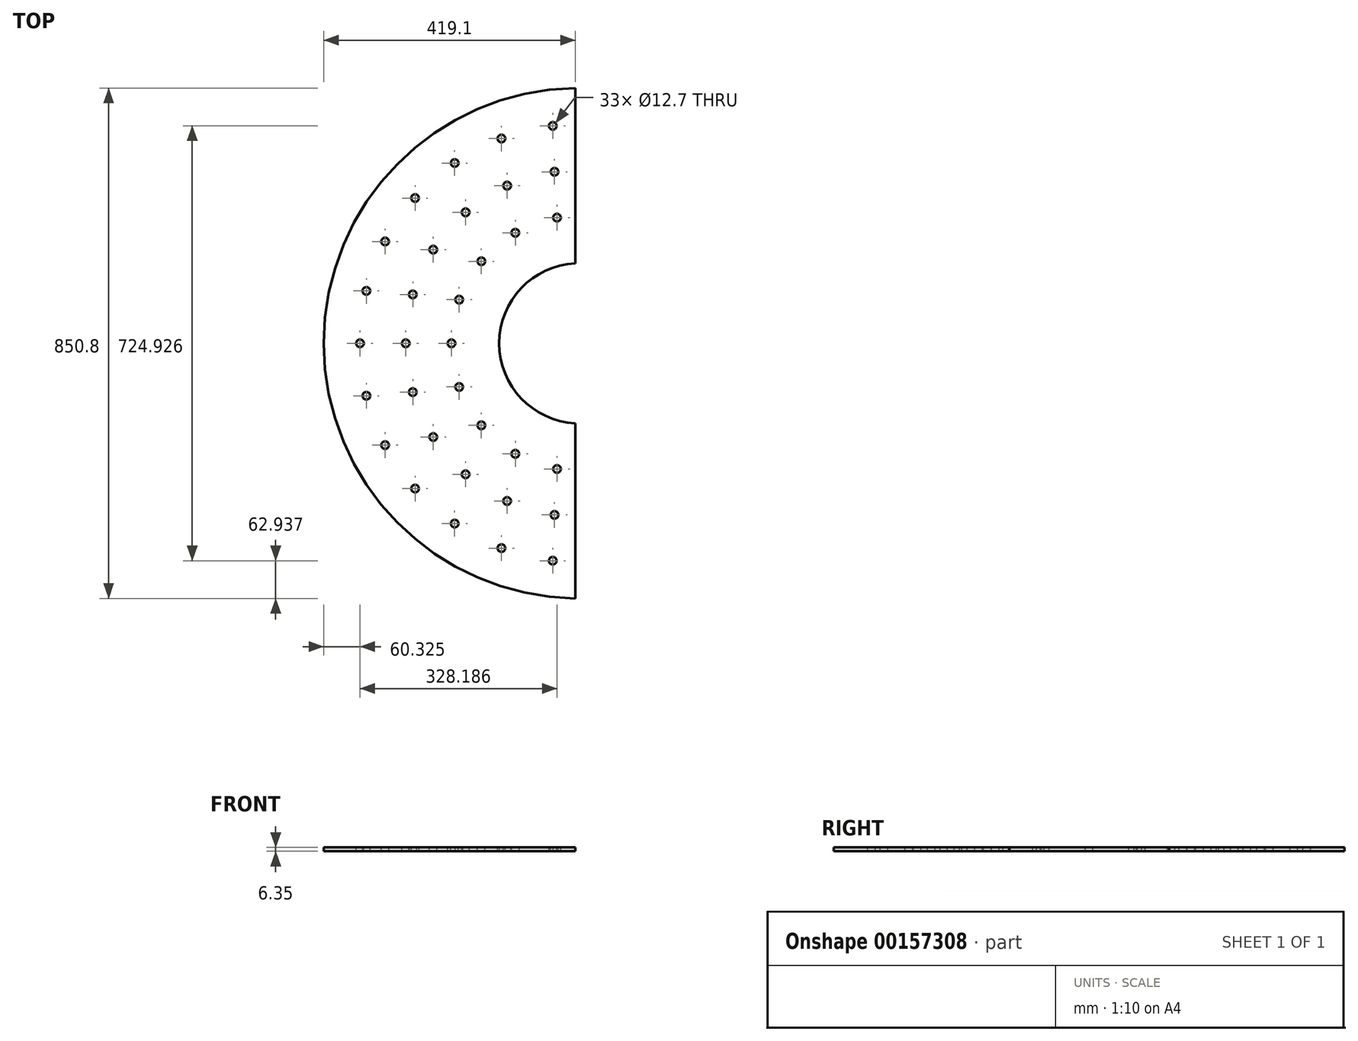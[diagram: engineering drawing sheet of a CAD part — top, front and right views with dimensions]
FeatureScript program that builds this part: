
annotation { "Feature Type Name" : "Feature", "Feature Type Description" : "" }
export const myFeature = defineFeature(function(context is Context, id is Id, definition is map)
    precondition{}
    {
        {
            var Q0;
            Q0=qCreatedBy(makeId("Top.planeOp"),FACE);
            var sketch = newSketch(context, id + "F0", { "sketchPlane" : qUnion([Q0])});
            skCircle(sketch, "E0", {"center": v(0, 0) * mm, "radius": 133.35 * mm});
            skCircle(sketch, "E1", {"center": v(0, 0) * mm, "radius": 425.45 * mm});
            skLineSegment(sketch, "E2", {"start": v(0, 133.35) * mm, "end": v(0, 425.45) * mm});
            skLineSegment(sketch, "E3", {"start": v(0, -133.35) * mm, "end": v(0, -425.45) * mm});
            skArc(sketch, "E4", {"start": v(0, -133.35) * mm, "mid": v(133.35, 0) * mm, "end": v(0, 133.35) * mm});
            skArc(sketch, "E5", {"start": v(0, -425.45) * mm, "mid": v(425.45, 0) * mm, "end": v(0, 425.45) * mm});
            skSolve(sketch);
        }
        {
            var Q0;
            Q0 = qSketchRegion(id + "F0", true);
            extrude(context, id + "F1", {"entities" : qUnion([Q0]), "depth" : 6.35 * mm});
        }
        {
            var Q0;
            Q0=makeQuery(id+"F1.opExtrude","CAP_FACE",FACE,{"disambiguationData":[OSD([sQuery(id+"F0.wireOp",EDGE,"E0"),sQuery(id+"F0.wireOp",EDGE,"E1")])],"isStart":false});
            var sketch = newSketch(context, id + "F2", { "sketchPlane" : qUnion([Q0])});
            skLineSegment(sketch, "E6", {"start": v(0, 133.35) * mm, "end": v(0, 425.45) * mm});
            skLineSegment(sketch, "E7", {"start": v(0, -133.35) * mm, "end": v(0, -425.45) * mm});
            skArc(sketch, "E8", {"start": v(0, -425.45) * mm, "mid": v(425.45, 0) * mm, "end": v(0, 425.45) * mm});
            skArc(sketch, "E9", {"start": v(0, -133.35) * mm, "mid": v(133.35, 0) * mm, "end": v(0, 133.35) * mm});
            skSolve(sketch);
        }
        {
            var Q0;
            Q0 = qSketchRegion(id + "F2", true);
            extrude(context, id + "F3", {"entities" : qUnion([Q0]), "operationType" : NewBodyOperationType.REMOVE, "endBound" : BoundingType.THROUGH_ALL, "oppositeDirection" : true, "depth" : 25.4 * mm});
        }
        {
            var Q0;
            Q0=makeQuery(id+"F1.opExtrude","CAP_FACE",FACE,{"disambiguationData":[OSD([sQuery(id+"F0.wireOp",EDGE,"E0"),sQuery(id+"F0.wireOp",EDGE,"E1")])],"isStart":false});
            var sketch = newSketch(context, id + "F4", { "sketchPlane" : qUnion([Q0])});
            skLineSegment(sketch, "E10.0", {"start": v(-31.75, 162.02) * mm, "end": v(-31.75, 392.42) * mm});
            skArc(sketch, "E10.1", {"start": v(-31.75, 162.02) * mm, "mid": v(-165.1, 0) * mm, "end": v(-31.75, -162.02) * mm});
            skLineSegment(sketch, "E10.2", {"start": v(-31.75, -162.02) * mm, "end": v(-31.75, -392.42) * mm});
            skArc(sketch, "E10.3", {"start": v(-31.75, 392.42) * mm, "mid": v(-393.7, 0) * mm, "end": v(-31.75, -392.42) * mm});
            skSolve(sketch);
        }
        {
            var Q0;
            Q0=makeQuery(id+"F4.imprint","IMPRINT",FACE,{"disambiguationData":[TD([[makeQuery(id+"F4.imprint","IMPRINT",EDGE,{"derivedFrom":sQuery(id+"F4.wireOp",EDGE,"E10.0")}),1.0]])]});
            var sketch = newSketch(context, id + "F5", { "sketchPlane" : qUnion([Q0])});
            skCircle(sketch, "E11", {"center": v(-288.93, 0) * mm, "radius": 6.35 * mm});
            skCircle(sketch, "E12.1.0", {"center": v(-277.22, -81.4) * mm, "radius": 6.35 * mm});
            skCircle(sketch, "E12.2.0", {"center": v(-243.06, -156.2) * mm, "radius": 6.35 * mm});
            skCircle(sketch, "E12.3.0", {"center": v(-189.2, -218.35) * mm, "radius": 6.35 * mm});
            skCircle(sketch, "E12.4.0", {"center": v(-120.02, -262.82) * mm, "radius": 6.35 * mm});
            skCircle(sketch, "E12.5.0", {"center": v(-41.12, -285.98) * mm, "radius": 6.35 * mm});
            skCircle(sketch, "E12.6.0", {"center": v(41.12, -285.98) * mm, "radius": 6.35 * mm});
            skCircle(sketch, "E12.7.0", {"center": v(120.02, -262.82) * mm, "radius": 6.35 * mm});
            skCircle(sketch, "E12.8.0", {"center": v(189.2, -218.35) * mm, "radius": 6.35 * mm});
            skCircle(sketch, "E12.9.0", {"center": v(243.06, -156.2) * mm, "radius": 6.35 * mm});
            skCircle(sketch, "E12.10.0", {"center": v(277.22, -81.4) * mm, "radius": 6.35 * mm});
            skCircle(sketch, "E12.11.0", {"center": v(288.93, 0) * mm, "radius": 6.35 * mm});
            skCircle(sketch, "E12.12.0", {"center": v(277.22, 81.4) * mm, "radius": 6.35 * mm});
            skCircle(sketch, "E12.13.0", {"center": v(243.06, 156.2) * mm, "radius": 6.35 * mm});
            skCircle(sketch, "E12.14.0", {"center": v(189.2, 218.35) * mm, "radius": 6.35 * mm});
            skCircle(sketch, "E12.15.0", {"center": v(120.02, 262.82) * mm, "radius": 6.35 * mm});
            skCircle(sketch, "E12.16.0", {"center": v(41.12, 285.98) * mm, "radius": 6.35 * mm});
            skCircle(sketch, "E12.17.0", {"center": v(-41.12, 285.98) * mm, "radius": 6.35 * mm});
            skCircle(sketch, "E12.18.0", {"center": v(-120.02, 262.82) * mm, "radius": 6.35 * mm});
            skCircle(sketch, "E12.19.0", {"center": v(-189.2, 218.35) * mm, "radius": 6.35 * mm});
            skCircle(sketch, "E12.20.0", {"center": v(-243.06, 156.2) * mm, "radius": 6.35 * mm});
            skCircle(sketch, "E12.21.0", {"center": v(-277.22, 81.4) * mm, "radius": 6.35 * mm});
            skPoint(sketch, "E12.center", {"position": v(0, 0) * mm});
            skSolve(sketch);
        }
        {
            var Q0;
            Q0 = qSketchRegion(id + "F5", true);
            extrude(context, id + "F6", {"entities" : qUnion([Q0]), "operationType" : NewBodyOperationType.REMOVE, "endBound" : BoundingType.THROUGH_ALL, "oppositeDirection" : true, "depth" : 25.4 * mm});
        }
        {
            var Q0;
            Q0=makeQuery(id+"F4.imprint","IMPRINT",FACE,{"disambiguationData":[TD([[makeQuery(id+"F4.imprint","IMPRINT",EDGE,{"derivedFrom":sQuery(id+"F4.wireOp",EDGE,"E10.0")}),1.0]])]});
            var sketch = newSketch(context, id + "F7", { "sketchPlane" : qUnion([Q0])});
            skCircle(sketch, "E13", {"center": v(-212.73, 0) * mm, "radius": 6.35 * mm});
            skCircle(sketch, "E14.1.0", {"center": v(-199.9, -72.76) * mm, "radius": 6.35 * mm});
            skCircle(sketch, "E14.2.0", {"center": v(-162.96, -136.74) * mm, "radius": 6.35 * mm});
            skCircle(sketch, "E14.3.0", {"center": v(-106.36, -184.23) * mm, "radius": 6.35 * mm});
            skCircle(sketch, "E14.4.0", {"center": v(-36.94, -209.5) * mm, "radius": 6.35 * mm});
            skCircle(sketch, "E14.5.0", {"center": v(36.94, -209.5) * mm, "radius": 6.35 * mm});
            skCircle(sketch, "E14.6.0", {"center": v(106.36, -184.23) * mm, "radius": 6.35 * mm});
            skCircle(sketch, "E14.7.0", {"center": v(162.96, -136.74) * mm, "radius": 6.35 * mm});
            skCircle(sketch, "E14.8.0", {"center": v(199.9, -72.76) * mm, "radius": 6.35 * mm});
            skCircle(sketch, "E14.9.0", {"center": v(212.73, 0) * mm, "radius": 6.35 * mm});
            skCircle(sketch, "E14.10.0", {"center": v(199.9, 72.76) * mm, "radius": 6.35 * mm});
            skCircle(sketch, "E14.11.0", {"center": v(162.96, 136.74) * mm, "radius": 6.35 * mm});
            skCircle(sketch, "E14.12.0", {"center": v(106.36, 184.23) * mm, "radius": 6.35 * mm});
            skCircle(sketch, "E14.13.0", {"center": v(36.94, 209.5) * mm, "radius": 6.35 * mm});
            skCircle(sketch, "E14.14.0", {"center": v(-36.94, 209.5) * mm, "radius": 6.35 * mm});
            skCircle(sketch, "E14.15.0", {"center": v(-106.36, 184.23) * mm, "radius": 6.35 * mm});
            skCircle(sketch, "E14.16.0", {"center": v(-162.96, 136.74) * mm, "radius": 6.35 * mm});
            skCircle(sketch, "E14.17.0", {"center": v(-199.9, 72.76) * mm, "radius": 6.35 * mm});
            skPoint(sketch, "E14.center", {"position": v(0, 0) * mm});
            skSolve(sketch);
        }
        {
            var Q0;
            Q0 = qSketchRegion(id + "F7", true);
            extrude(context, id + "F8", {"entities" : qUnion([Q0]), "operationType" : NewBodyOperationType.REMOVE, "endBound" : BoundingType.THROUGH_ALL, "oppositeDirection" : true, "depth" : 25.4 * mm});
        }
        {
            var Q0;
            Q0=makeQuery(id+"F4.imprint","IMPRINT",FACE,{"disambiguationData":[TD([[makeQuery(id+"F4.imprint","IMPRINT",EDGE,{"derivedFrom":sQuery(id+"F4.wireOp",EDGE,"E10.0")}),1.0]])]});
            var sketch = newSketch(context, id + "F9", { "sketchPlane" : qUnion([Q0])});
            skCircle(sketch, "E15", {"center": v(-365.13, 0) * mm, "radius": 6.35 * mm});
            skCircle(sketch, "E16.1.0", {"center": v(-354.52, -87.38) * mm, "radius": 6.35 * mm});
            skCircle(sketch, "E16.2.0", {"center": v(-323.3, -169.68) * mm, "radius": 6.35 * mm});
            skCircle(sketch, "E16.3.0", {"center": v(-273.3, -242.12) * mm, "radius": 6.35 * mm});
            skCircle(sketch, "E16.4.0", {"center": v(-207.41, -300.5) * mm, "radius": 6.35 * mm});
            skCircle(sketch, "E16.5.0", {"center": v(-129.48, -341.4) * mm, "radius": 6.35 * mm});
            skCircle(sketch, "E16.6.0", {"center": v(-44.01, -362.46) * mm, "radius": 6.35 * mm});
            skCircle(sketch, "E16.7.0", {"center": v(44.01, -362.46) * mm, "radius": 6.35 * mm});
            skCircle(sketch, "E16.8.0", {"center": v(129.48, -341.4) * mm, "radius": 6.35 * mm});
            skCircle(sketch, "E16.9.0", {"center": v(207.41, -300.5) * mm, "radius": 6.35 * mm});
            skCircle(sketch, "E16.10.0", {"center": v(273.3, -242.12) * mm, "radius": 6.35 * mm});
            skCircle(sketch, "E16.11.0", {"center": v(323.3, -169.68) * mm, "radius": 6.35 * mm});
            skCircle(sketch, "E16.12.0", {"center": v(354.52, -87.38) * mm, "radius": 6.35 * mm});
            skCircle(sketch, "E16.13.0", {"center": v(365.13, 0) * mm, "radius": 6.35 * mm});
            skCircle(sketch, "E16.14.0", {"center": v(354.52, 87.38) * mm, "radius": 6.35 * mm});
            skCircle(sketch, "E16.15.0", {"center": v(323.3, 169.68) * mm, "radius": 6.35 * mm});
            skCircle(sketch, "E16.16.0", {"center": v(273.3, 242.12) * mm, "radius": 6.35 * mm});
            skCircle(sketch, "E16.17.0", {"center": v(207.41, 300.5) * mm, "radius": 6.35 * mm});
            skCircle(sketch, "E16.18.0", {"center": v(129.48, 341.4) * mm, "radius": 6.35 * mm});
            skCircle(sketch, "E16.19.0", {"center": v(44.01, 362.46) * mm, "radius": 6.35 * mm});
            skCircle(sketch, "E16.20.0", {"center": v(-44.01, 362.46) * mm, "radius": 6.35 * mm});
            skCircle(sketch, "E16.21.0", {"center": v(-129.48, 341.4) * mm, "radius": 6.35 * mm});
            skCircle(sketch, "E16.22.0", {"center": v(-207.41, 300.5) * mm, "radius": 6.35 * mm});
            skCircle(sketch, "E16.23.0", {"center": v(-273.3, 242.12) * mm, "radius": 6.35 * mm});
            skCircle(sketch, "E16.24.0", {"center": v(-323.3, 169.68) * mm, "radius": 6.35 * mm});
            skCircle(sketch, "E16.25.0", {"center": v(-354.52, 87.38) * mm, "radius": 6.35 * mm});
            skPoint(sketch, "E16.center", {"position": v(0, 0) * mm});
            skSolve(sketch);
        }
        {
            var Q0;
            Q0 = qSketchRegion(id + "F9", true);
            extrude(context, id + "F10", {"entities" : qUnion([Q0]), "operationType" : NewBodyOperationType.REMOVE, "endBound" : BoundingType.THROUGH_ALL, "oppositeDirection" : true, "depth" : 25.4 * mm});
        }
        {
            var Q0;
            Q0=qCreatedBy(makeId("Top.planeOp"),FACE);
            var sketch = newSketch(context, id + "F11", { "sketchPlane" : qUnion([Q0])});
            skLineSegment(sketch, "E17.bottom", {"start": v(0, 473.68) * mm, "end": v(-6.35, 473.68) * mm});
            skLineSegment(sketch, "E17.top", {"start": v(0, -464.64) * mm, "end": v(-6.35, -464.64) * mm});
            skLineSegment(sketch, "E17.left", {"start": v(0, 473.68) * mm, "end": v(0, -464.64) * mm});
            skLineSegment(sketch, "E17.right", {"start": v(-6.35, 473.68) * mm, "end": v(-6.35, -464.64) * mm});
            skSolve(sketch);
        }
        {
            var Q0;
            Q0 = qSketchRegion(id + "F11", true);
            extrude(context, id + "F12", {"entities" : qUnion([Q0]), "operationType" : NewBodyOperationType.REMOVE, "endBound" : BoundingType.THROUGH_ALL, "depth" : 25.4 * mm});
        }
    });
